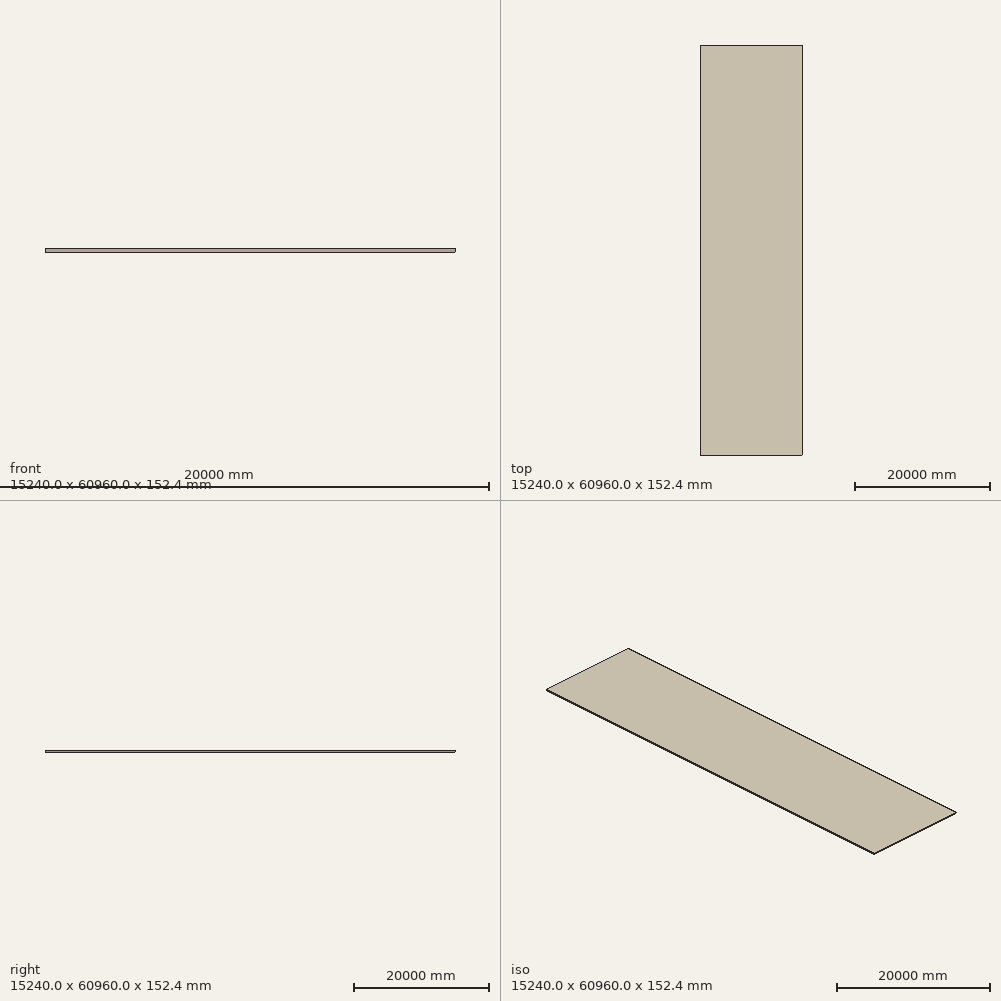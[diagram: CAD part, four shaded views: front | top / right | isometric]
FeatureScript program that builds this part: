
annotation { "Feature Type Name" : "Feature", "Feature Type Description" : "" }
export const myFeature = defineFeature(function(context is Context, id is Id, definition is map)
    precondition{}
    {
        {
            var Q0;
            Q0=qCreatedBy(makeId("Top.planeOp"),FACE);
            var sketch = newSketch(context, id + "F0", { "sketchPlane" : qUnion([Q0])});
            skLineSegment(sketch, "E0.bottom", {"start": v(7620, 30480) * mm, "end": v(-7620, 30480) * mm});
            skLineSegment(sketch, "E0.top", {"start": v(7620, -30480) * mm, "end": v(-7620, -30480) * mm});
            skLineSegment(sketch, "E0.left", {"start": v(7620, 30480) * mm, "end": v(7620, -30480) * mm});
            skLineSegment(sketch, "E0.right", {"start": v(-7620, 30480) * mm, "end": v(-7620, -30480) * mm});
            skPoint(sketch, "E0.middle", {"position": v(0, 0) * mm});
            skSolve(sketch);
        }
        {
            var Q0;
            Q0 = qSketchRegion(id + "F0", true);
            extrude(context, id + "F1", {"entities" : qUnion([Q0]), "depth" : 152.4 * mm, "offsetDistance" : 25.4 * mm});
        }
    });
